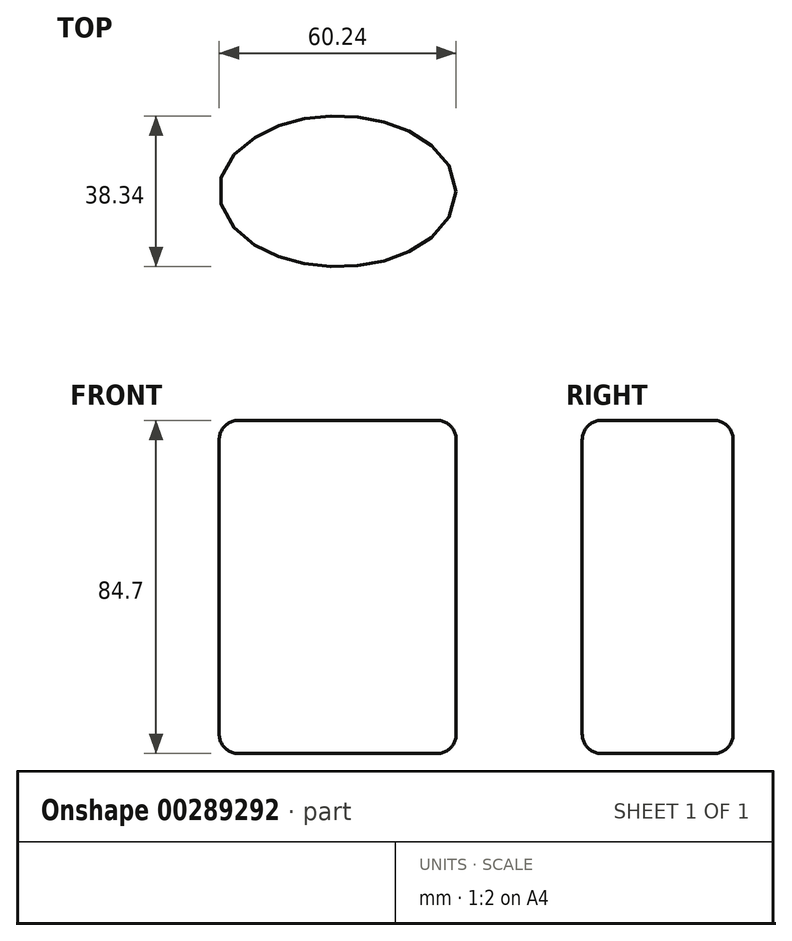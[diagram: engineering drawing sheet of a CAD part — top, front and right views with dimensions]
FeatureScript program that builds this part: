
annotation { "Feature Type Name" : "Feature", "Feature Type Description" : "" }
export const myFeature = defineFeature(function(context is Context, id is Id, definition is map)
    precondition{}
    {
        {
            var Q0;
            Q0=qCreatedBy(makeId("Top.planeOp"),FACE);
            var sketch = newSketch(context, id + "F0", { "sketchPlane" : qUnion([Q0])});
            skEllipse(sketch, "E0", {"center": v(0, 0) * mm, "majorRadius": 30.12 * mm, "minorRadius": 19.17 * mm, "majorAxis": v(1, 0)});
            skEllipse(sketch, "E1", {"center": v(-50.36, 0) * mm, "majorRadius": 9.11 * mm, "minorRadius": 7.6 * mm, "majorAxis": v(1, 0)});
            skEllipse(sketch, "E2.MirrorC", {"center": v(50.36, 0) * mm, "majorRadius": 9.11 * mm, "minorRadius": 7.6 * mm, "majorAxis": v(-1, 0)});
            skSolve(sketch);
        }
        {
            var Q0;
            Q0=makeQuery(id+"F0.imprint","IMPRINT",FACE,{"disambiguationData":[TD([[makeQuery(id+"F0.imprint","IMPRINT",EDGE,{"derivedFrom":sQuery(id+"F0.wireOp",EDGE,"E0")}),1.0]])]});
            extrude(context, id + "F1", {"entities" : qUnion([Q0]), "depth" : 84.7 * mm});
        }
        {
            var Q0;
            Q0=makeQuery(id+"F1.opExtrude","CAP_EDGE",EDGE,{"disambiguationData":[OSD([sQuery(id+"F0.wireOp",EDGE,"E0")])],"isStart":false});
            var Q1;
            Q1=makeQuery(id+"F1.opExtrude","CAP_EDGE",EDGE,{"disambiguationData":[OSD([sQuery(id+"F0.wireOp",EDGE,"E0")])],"isStart":true});
            fillet(context, id + "F2", {"entities" : qUnion([Q0, Q1]), "radius" : 5 * mm, "tangentPropagation" : true, "allowEdgeOverflow" : false});
        }
    });
